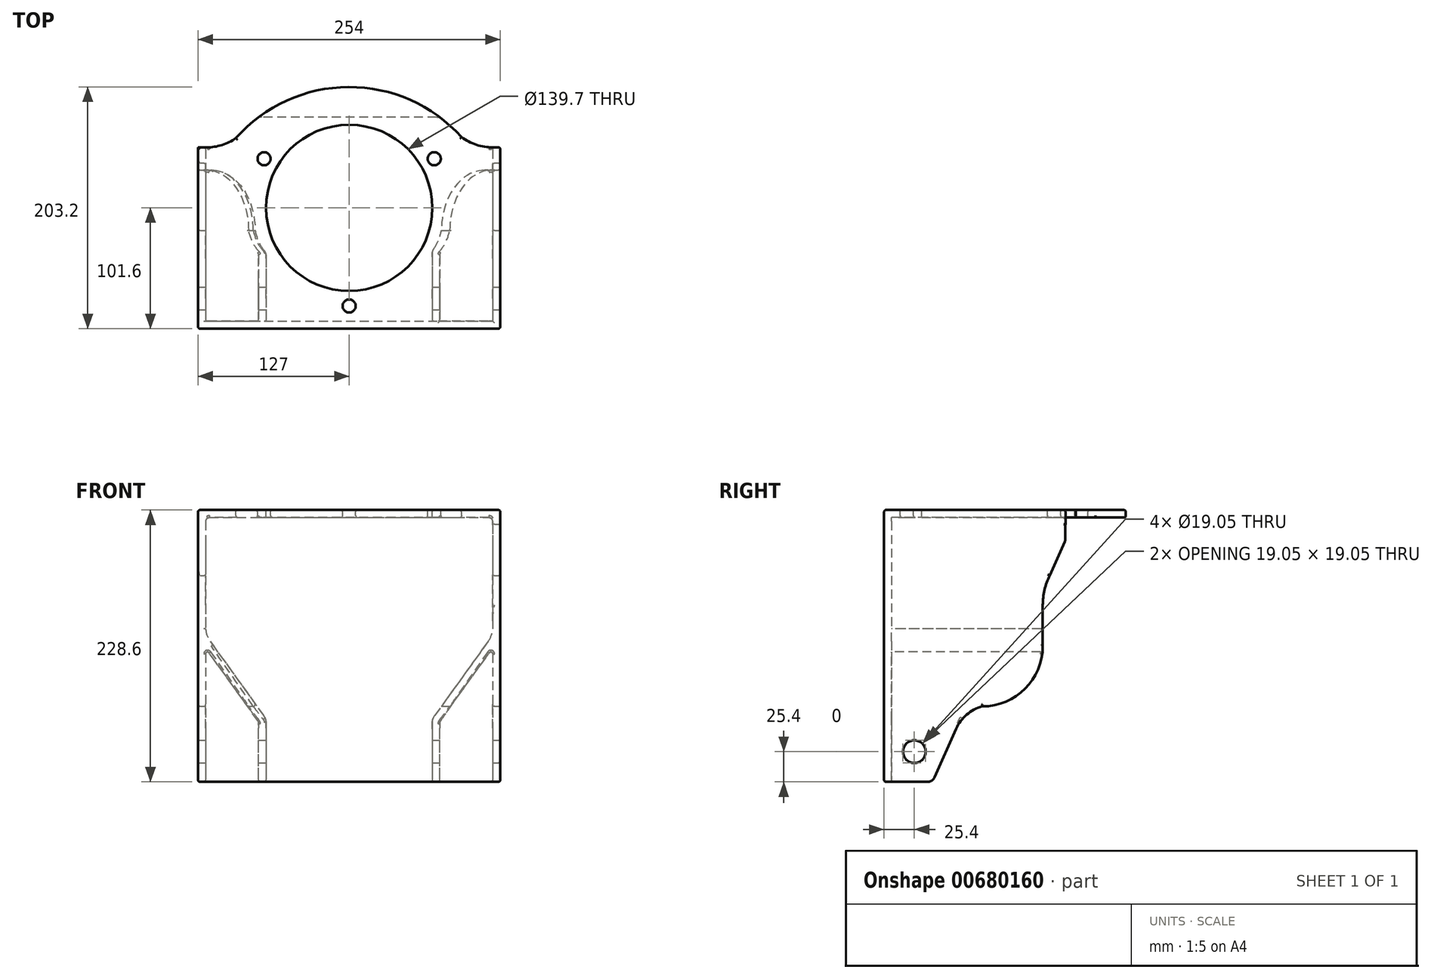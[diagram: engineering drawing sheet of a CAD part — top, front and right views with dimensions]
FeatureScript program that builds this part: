
annotation { "Feature Type Name" : "Feature", "Feature Type Description" : "" }
export const myFeature = defineFeature(function(context is Context, id is Id, definition is map)
    precondition{}
    {
        {
            var Q0;
            Q0=qCreatedBy(makeId("Right.planeOp"),FACE);
            var sketch = newSketch(context, id + "F0", { "sketchPlane" : qUnion([Q0])});
            skLineSegment(sketch, "E0", {"start": v(75.65, 74.97) * mm, "end": v(63.05, 46.62) * mm});
            skLineSegment(sketch, "E1", {"start": v(57.15, 21.64) * mm, "end": v(57.15, -12.7) * mm});
            skLineSegment(sketch, "E2", {"start": v(-39.56, -127) * mm, "end": v(-76.2, -127) * mm});
            skLineSegment(sketch, "E3", {"start": v(-76.2, -127) * mm, "end": v(-76.2, 101.6) * mm});
            skLineSegment(sketch, "E4", {"start": v(-76.2, 101.6) * mm, "end": v(127, 101.6) * mm});
            skLineSegment(sketch, "E5", {"start": v(76.2, 88.88) * mm, "end": v(76.2, 77.55) * mm});
            skArc(sketch, "E6.filletArc", {"start": v(6.35, -63.5) * mm, "mid": v(42.27, -48.62) * mm, "end": v(57.15, -12.7) * mm});
            skLineSegment(sketch, "E7", {"start": v(-15.7, -82.38) * mm, "end": v(-33.75, -123.22) * mm});
            skArc(sketch, "E8.filletArc", {"start": v(-39.56, -127) * mm, "mid": v(-36.1, -125.97) * mm, "end": v(-33.75, -123.22) * mm});
            skPoint(sketch, "E9.visualSharp", {"position": v(76.2, 76.2) * mm});
            skPoint(sketch, "E10.visualSharp", {"position": v(76.2, 101.6) * mm});
            skArc(sketch, "E11", {"start": v(57.15, 21.64) * mm, "mid": v(58.65, 34.47) * mm, "end": v(63.05, 46.62) * mm});
            skArc(sketch, "E12", {"start": v(-15.7, -82.38) * mm, "mid": v(-6.81, -70.44) * mm, "end": v(6.35, -63.5) * mm});
            skArc(sketch, "E13", {"start": v(75.65, 74.97) * mm, "mid": v(76.06, 76.23) * mm, "end": v(76.2, 77.55) * mm});
            skLineSegment(sketch, "E14", {"start": v(82.55, 95.23) * mm, "end": v(127, 95.23) * mm});
            skLineSegment(sketch, "E15", {"start": v(127, 95.23) * mm, "end": v(127, 101.6) * mm});
            skPoint(sketch, "E16.visualSharp", {"position": v(76.2, 95.23) * mm});
            skArc(sketch, "E16.filletArc", {"start": v(82.55, 95.23) * mm, "mid": v(78.06, 93.37) * mm, "end": v(76.2, 88.88) * mm});
            skSolve(sketch);
        }
        {
            var Q0;
            Q0 = qSketchRegion(id + "F0", true);
            extrude(context, id + "F1", {"entities" : qUnion([Q0]), "endBound" : BoundingType.SYMMETRIC, "oppositeDirection" : true, "depth" : 254 * mm, "offsetDistance" : 25.4 * mm});
        }
        {
            var Q0;
            Q0=qCreatedBy(makeId("Front.planeOp"),FACE);
            var sketch = newSketch(context, id + "F2", { "sketchPlane" : qUnion([Q0])});
            skLineSegment(sketch, "E17", {"start": v(120.65, 92.08) * mm, "end": v(120.65, 1.64) * mm});
            skLineSegment(sketch, "E18", {"start": v(116.8, -8.9) * mm, "end": v(71.05, -72.5) * mm});
            skLineSegment(sketch, "E19", {"start": v(69.85, -76.2) * mm, "end": v(69.85, -127) * mm});
            skLineSegment(sketch, "E20", {"start": v(69.85, -127) * mm, "end": v(0, -127) * mm});
            skArc(sketch, "E21", {"start": v(69.85, -76.2) * mm, "mid": v(70.16, -74.25) * mm, "end": v(71.05, -72.5) * mm});
            skArc(sketch, "E22", {"start": v(116.8, -8.9) * mm, "mid": v(119.45, -3.9) * mm, "end": v(120.65, 1.64) * mm});
            skArc(sketch, "E23.MirrorCS", {"start": v(-116.8, -8.9) * mm, "mid": v(-119.45, -3.9) * mm, "end": v(-120.65, 1.64) * mm});
            skArc(sketch, "E24.MirrorCS", {"start": v(-69.85, -76.2) * mm, "mid": v(-70.16, -74.25) * mm, "end": v(-71.05, -72.5) * mm});
            skLineSegment(sketch, "E25.MirrorCS", {"start": v(-69.85, -127) * mm, "end": v(0, -127) * mm});
            skLineSegment(sketch, "E26.MirrorCS", {"start": v(-69.85, -76.2) * mm, "end": v(-69.85, -127) * mm});
            skLineSegment(sketch, "E27.MirrorCS", {"start": v(-116.8, -8.9) * mm, "end": v(-71.05, -72.5) * mm});
            skLineSegment(sketch, "E28.MirrorCS", {"start": v(-120.65, 92.08) * mm, "end": v(-120.65, 1.64) * mm});
            skLineSegment(sketch, "E29", {"start": v(-117.48, 95.25) * mm, "end": v(117.47, 95.25) * mm});
            skArc(sketch, "E30", {"start": v(120.65, 92.08) * mm, "mid": v(119.72, 94.32) * mm, "end": v(117.47, 95.25) * mm});
            skArc(sketch, "E31", {"start": v(-120.65, 92.08) * mm, "mid": v(-119.72, 94.32) * mm, "end": v(-117.48, 95.25) * mm});
            skSolve(sketch);
        }
        {
            var Q0;
            Q0 = qSketchRegion(id + "F2", true);
            extrude(context, id + "F3", {"entities" : qUnion([Q0]), "operationType" : NewBodyOperationType.REMOVE, "endBound" : BoundingType.SYMMETRIC, "oppositeDirection" : true, "depth" : 139.7 * mm, "offsetDistance" : 25.4 * mm});
        }
        {
            var Q0;
            Q0 = qSketchRegion(id + "F2", true);
            extrude(context, id + "F4", {"entities" : qUnion([Q0]), "operationType" : NewBodyOperationType.REMOVE, "oppositeDirection" : true, "depth" : 101.6 * mm, "offsetDistance" : 25.4 * mm});
        }
        {
            var Q0;
            Q0=makeQuery(id+"F1.opExtrude","SWEPT_FACE",FACE,{"disambiguationData":[OSD([sQuery(id+"F0.wireOp",EDGE,"E4")])]});
            var sketch = newSketch(context, id + "F5", { "sketchPlane" : qUnion([Q0])});
            skArc(sketch, "E32", {"start": v(94.46, 84.9) * mm, "mid": v(-0.55, 127) * mm, "end": v(-95.19, 84.07) * mm});
            skLineSegment(sketch, "E33", {"start": v(-127.06, 76.2) * mm, "end": v(-119.85, 76.2) * mm});
            skArc(sketch, "E34", {"start": v(-119.85, 76.2) * mm, "mid": v(-106.9, 78.22) * mm, "end": v(-95.19, 84.07) * mm});
            skLineSegment(sketch, "E35", {"start": v(127.01, 76.25) * mm, "end": v(120.8, 76.25) * mm});
            skArc(sketch, "E36", {"start": v(120.8, 76.25) * mm, "mid": v(106.94, 78.46) * mm, "end": v(94.46, 84.9) * mm});
            skLineSegment(sketch, "E37", {"start": v(-127.06, 76.2) * mm, "end": v(-127, 127) * mm});
            skLineSegment(sketch, "E38", {"start": v(-127, 127) * mm, "end": v(127, 127) * mm});
            skLineSegment(sketch, "E39", {"start": v(127, 127) * mm, "end": v(127.01, 76.25) * mm});
            skSolve(sketch);
        }
        {
            var Q0;
            Q0 = qSketchRegion(id + "F5", true);
            extrude(context, id + "F6", {"entities" : qUnion([Q0]), "operationType" : NewBodyOperationType.REMOVE, "oppositeDirection" : true, "depth" : 19.05 * mm, "offsetDistance" : 25.4 * mm});
        }
        {
            var Q0;
            Q0=qCreatedBy(makeId("Front.planeOp"),FACE);
            var sketch = newSketch(context, id + "F7", { "sketchPlane" : qUnion([Q0])});
            skLineSegment(sketch, "E40", {"start": v(120.65, -19.35) * mm, "end": v(120.65, -135.84) * mm});
            skLineSegment(sketch, "E41", {"start": v(120.65, -135.84) * mm, "end": v(76.2, -135.84) * mm});
            skLineSegment(sketch, "E42", {"start": v(76.2, -135.84) * mm, "end": v(76.2, -77.22) * mm});
            skLineSegment(sketch, "E43", {"start": v(76.8, -75.37) * mm, "end": v(117.77, -18.42) * mm});
            skPoint(sketch, "E44.visualSharp", {"position": v(120.65, -14.42) * mm});
            skArc(sketch, "E44.filletArc", {"start": v(120.65, -19.35) * mm, "mid": v(119.55, -17.84) * mm, "end": v(117.77, -18.42) * mm});
            skPoint(sketch, "E45.visualSharp", {"position": v(76.2, -76.2) * mm});
            skArc(sketch, "E45.filletArc", {"start": v(76.8, -75.37) * mm, "mid": v(76.35, -76.25) * mm, "end": v(76.2, -77.22) * mm});
            skArc(sketch, "E46.MirrorCS", {"start": v(-120.65, -19.35) * mm, "mid": v(-119.55, -17.84) * mm, "end": v(-117.77, -18.42) * mm});
            skArc(sketch, "E47.MirrorCS", {"start": v(-76.8, -75.37) * mm, "mid": v(-76.35, -76.25) * mm, "end": v(-76.2, -77.22) * mm});
            skLineSegment(sketch, "E48.MirrorCS", {"start": v(-120.65, -135.84) * mm, "end": v(-76.2, -135.84) * mm});
            skPoint(sketch, "E49.MirrorP", {"position": v(-76.2, -76.2) * mm});
            skLineSegment(sketch, "E50.MirrorCS", {"start": v(-120.65, -19.35) * mm, "end": v(-120.65, -135.84) * mm});
            skPoint(sketch, "E51.MirrorP", {"position": v(-120.65, -14.42) * mm});
            skLineSegment(sketch, "E52.MirrorCS", {"start": v(-76.8, -75.37) * mm, "end": v(-117.77, -18.42) * mm});
            skLineSegment(sketch, "E53.MirrorCS", {"start": v(-76.2, -135.84) * mm, "end": v(-76.2, -77.22) * mm});
            skSolve(sketch);
        }
        {
            var Q0;
            Q0 = qSketchRegion(id + "F7", true);
            extrude(context, id + "F8", {"entities" : qUnion([Q0]), "operationType" : NewBodyOperationType.REMOVE, "endBound" : BoundingType.SYMMETRIC, "oppositeDirection" : true, "depth" : 139.7 * mm, "offsetDistance" : 25.4 * mm});
        }
        {
            var Q0;
            Q0=makeQuery(id+"F1.opExtrude","SWEPT_FACE",FACE,{"disambiguationData":[OSD([sQuery(id+"F0.wireOp",EDGE,"E4")])]});
            var sketch = newSketch(context, id + "F9", { "sketchPlane" : qUnion([Q0])});
            skCircle(sketch, "E54", {"center": v(0, 25.4) * mm, "radius": 69.85 * mm});
            skCircle(sketch, "E55", {"center": v(-71.5, 66.68) * mm, "radius": 5.52 * mm});
            skCircle(sketch, "E56", {"center": v(71.5, 66.67) * mm, "radius": 5.52 * mm});
            skCircle(sketch, "E57", {"center": v(0, -57.15) * mm, "radius": 5.52 * mm});
            skSolve(sketch);
        }
        {
            var Q0;
            Q0 = qSketchRegion(id + "F9", true);
            extrude(context, id + "F10", {"entities" : qUnion([Q0]), "operationType" : NewBodyOperationType.REMOVE, "oppositeDirection" : true, "depth" : 6.86 * mm, "offsetDistance" : 25.4 * mm});
        }
        {
            var Q0;
            Q0=makeQuery(id+"F1.opExtrude","CAP_FACE",FACE,{"disambiguationData":[OSD([sQuery(id+"F0.wireOp",EDGE,"E0"),sQuery(id+"F0.wireOp",EDGE,"E1"),sQuery(id+"F0.wireOp",EDGE,"E2"),sQuery(id+"F0.wireOp",EDGE,"E3"),sQuery(id+"F0.wireOp",EDGE,"E4"),sQuery(id+"F0.wireOp",EDGE,"E5"),sQuery(id+"F0.wireOp",EDGE,"E6.filletArc"),sQuery(id+"F0.wireOp",EDGE,"E7"),sQuery(id+"F0.wireOp",EDGE,"E8.filletArc"),sQuery(id+"F0.wireOp",EDGE,"E11"),sQuery(id+"F0.wireOp",EDGE,"E12"),sQuery(id+"F0.wireOp",EDGE,"E13"),sQuery(id+"F0.wireOp",EDGE,"E14"),sQuery(id+"F0.wireOp",EDGE,"E15"),sQuery(id+"F0.wireOp",EDGE,"E16.filletArc")])],"isStart":true});
            var sketch = newSketch(context, id + "F11", { "sketchPlane" : qUnion([Q0])});
            skCircle(sketch, "E58", {"center": v(-50.8, -101.6) * mm, "radius": 9.53 * mm});
            skSolve(sketch);
        }
        {
            var Q0;
            Q0 = qSketchRegion(id + "F11", true);
            extrude(context, id + "F12", {"entities" : qUnion([Q0]), "operationType" : NewBodyOperationType.REMOVE, "endBound" : BoundingType.THROUGH_ALL, "oppositeDirection" : true, "depth" : 25.4 * mm, "offsetDistance" : 25.4 * mm});
        }
        {
            var Q0;
            Q0=makeQuery(id+"F10.boolean.opBoolean","COPY",EDGE,{"derivedFrom":makeQuery(id+"F10.opExtrude","CAP_EDGE",EDGE,{"disambiguationData":[OSD([sQuery(id+"F9.wireOp",EDGE,"E54")])],"isStart":true})});
            var Q1;
            Q1=makeQuery(id+"F10.boolean.opBoolean","COPY",EDGE,{"derivedFrom":makeQuery(id+"F10.opExtrude","CAP_EDGE",EDGE,{"disambiguationData":[OSD([sQuery(id+"F9.wireOp",EDGE,"E55")])],"isStart":true})});
            var Q2;
            Q2=makeQuery(id+"F10.boolean.opBoolean","COPY",EDGE,{"derivedFrom":makeQuery(id+"F10.opExtrude","CAP_EDGE",EDGE,{"disambiguationData":[OSD([sQuery(id+"F9.wireOp",EDGE,"E56")])],"isStart":true})});
            var Q3;
            {var subQ0=sQuery(id+"F2.wireOp",EDGE,"E29");Q3=makeQuery(id+"F10.boolean.opBoolean","INTERSECT",EDGE,{"derivedFrom":[makeQuery(id+"F4.boolean.opBoolean","MERGE",FACE,{"derivedFrom":[makeQuery(id+"F3.boolean.opBoolean","COPY",FACE,{"derivedFrom":makeQuery(id+"F3.opExtrude","SWEPT_FACE",FACE,{"disambiguationData":[OSD([subQ0])]})}),makeQuery(id+"F4.opExtrude","SWEPT_FACE",FACE,{"disambiguationData":[OSD([subQ0])]})]}),makeQuery(id+"F10.opExtrude","SWEPT_FACE",FACE,{"disambiguationData":[OSD([sQuery(id+"F9.wireOp",EDGE,"E56")])]})]});}
            var Q4;
            Q4=makeQuery(id+"F10.boolean.opBoolean","COPY",EDGE,{"derivedFrom":makeQuery(id+"F10.opExtrude","CAP_EDGE",EDGE,{"disambiguationData":[OSD([sQuery(id+"F9.wireOp",EDGE,"E57")])],"isStart":true})});
            var Q5;
            {var subQ0=sQuery(id+"F2.wireOp",EDGE,"E29");Q5=makeQuery(id+"F10.boolean.opBoolean","INTERSECT",EDGE,{"derivedFrom":[makeQuery(id+"F4.boolean.opBoolean","MERGE",FACE,{"derivedFrom":[makeQuery(id+"F3.boolean.opBoolean","COPY",FACE,{"derivedFrom":makeQuery(id+"F3.opExtrude","SWEPT_FACE",FACE,{"disambiguationData":[OSD([subQ0])]})}),makeQuery(id+"F4.opExtrude","SWEPT_FACE",FACE,{"disambiguationData":[OSD([subQ0])]})]}),makeQuery(id+"F10.opExtrude","SWEPT_FACE",FACE,{"disambiguationData":[OSD([sQuery(id+"F9.wireOp",EDGE,"E57")])]})]});}
            var Q6;
            {var subQ0=sQuery(id+"F2.wireOp",EDGE,"E29");Q6=makeQuery(id+"F10.boolean.opBoolean","INTERSECT",EDGE,{"derivedFrom":[makeQuery(id+"F4.boolean.opBoolean","MERGE",FACE,{"derivedFrom":[makeQuery(id+"F3.boolean.opBoolean","COPY",FACE,{"derivedFrom":makeQuery(id+"F3.opExtrude","SWEPT_FACE",FACE,{"disambiguationData":[OSD([subQ0])]})}),makeQuery(id+"F4.opExtrude","SWEPT_FACE",FACE,{"disambiguationData":[OSD([subQ0])]})]}),makeQuery(id+"F10.opExtrude","SWEPT_FACE",FACE,{"disambiguationData":[OSD([sQuery(id+"F9.wireOp",EDGE,"E55")])]})]});}
            var Q7;
            Q7=makeQuery(id+"F1.opExtrude","CAP_EDGE",EDGE,{"disambiguationData":[OSD([sQuery(id+"F0.wireOp",EDGE,"E4")])],"isStart":true});
            var Q8;
            Q8=makeQuery(id+"F1.opExtrude","SWEPT_EDGE",EDGE,{"disambiguationData":[OSD([sQuery(id+"F0.wireOp",EDGE,"E3"),sQuery(id+"F0.wireOp",EDGE,"E4")])]});
            var Q9;
            Q9=makeQuery(id+"F1.opExtrude","CAP_EDGE",EDGE,{"disambiguationData":[OSD([sQuery(id+"F0.wireOp",EDGE,"E4")])],"isStart":false});
            var Q10;
            Q10=makeQuery(id+"F6.boolean.opBoolean","COPY",EDGE,{"derivedFrom":makeQuery(id+"F6.opExtrude","CAP_EDGE",EDGE,{"disambiguationData":[OSD([sQuery(id+"F5.wireOp",EDGE,"E33")])],"isStart":true})});
            var Q11;
            Q11=makeQuery(id+"F1.opExtrude","SWEPT_FACE",FACE,{"disambiguationData":[OSD([sQuery(id+"F0.wireOp",EDGE,"E4")])]});
            var Q12;
            {var subQ0=sQuery(id+"F2.wireOp",EDGE,"E30");Q12=makeQuery(id+"F6.boolean.opBoolean","INTERSECT",EDGE,{"derivedFrom":[makeQuery(id+"F4.boolean.opBoolean","MERGE",FACE,{"derivedFrom":[makeQuery(id+"F3.boolean.opBoolean","COPY",FACE,{"derivedFrom":makeQuery(id+"F3.opExtrude","SWEPT_FACE",FACE,{"disambiguationData":[OSD([subQ0])]})}),makeQuery(id+"F4.opExtrude","SWEPT_FACE",FACE,{"disambiguationData":[OSD([subQ0])]})]}),makeQuery(id+"F6.opExtrude","SWEPT_FACE",FACE,{"disambiguationData":[OSD([sQuery(id+"F5.wireOp",EDGE,"E36")])]})]});}
            var Q13;
            {var subQ0=sQuery(id+"F2.wireOp",EDGE,"E29");Q13=makeQuery(id+"F6.boolean.opBoolean","INTERSECT",EDGE,{"derivedFrom":[makeQuery(id+"F4.boolean.opBoolean","MERGE",FACE,{"derivedFrom":[makeQuery(id+"F3.boolean.opBoolean","COPY",FACE,{"derivedFrom":makeQuery(id+"F3.opExtrude","SWEPT_FACE",FACE,{"disambiguationData":[OSD([subQ0])]})}),makeQuery(id+"F4.opExtrude","SWEPT_FACE",FACE,{"disambiguationData":[OSD([subQ0])]})]}),makeQuery(id+"F6.opExtrude","SWEPT_FACE",FACE,{"disambiguationData":[OSD([sQuery(id+"F5.wireOp",EDGE,"E36")])]})]});}
            var Q14;
            Q14=makeQuery(id+"F4.boolean.opBoolean","INTERSECT",EDGE,{"derivedFrom":[makeQuery(id+"F1.opExtrude","SWEPT_FACE",FACE,{"disambiguationData":[OSD([sQuery(id+"F0.wireOp",EDGE,"E0")])]}),makeQuery(id+"F4.opExtrude","SWEPT_FACE",FACE,{"disambiguationData":[OSD([sQuery(id+"F2.wireOp",EDGE,"E17")])]})]});
            var Q15;
            Q15=makeQuery(id+"F1.opExtrude","CAP_FACE",FACE,{"disambiguationData":[OSD([sQuery(id+"F0.wireOp",EDGE,"E0"),sQuery(id+"F0.wireOp",EDGE,"E1"),sQuery(id+"F0.wireOp",EDGE,"E2"),sQuery(id+"F0.wireOp",EDGE,"E3"),sQuery(id+"F0.wireOp",EDGE,"E4"),sQuery(id+"F0.wireOp",EDGE,"E5"),sQuery(id+"F0.wireOp",EDGE,"E6.filletArc"),sQuery(id+"F0.wireOp",EDGE,"E7"),sQuery(id+"F0.wireOp",EDGE,"E8.filletArc"),sQuery(id+"F0.wireOp",EDGE,"E11"),sQuery(id+"F0.wireOp",EDGE,"E12"),sQuery(id+"F0.wireOp",EDGE,"E13"),sQuery(id+"F0.wireOp",EDGE,"E14"),sQuery(id+"F0.wireOp",EDGE,"E15"),sQuery(id+"F0.wireOp",EDGE,"E16.filletArc")])],"isStart":true});
            var Q16;
            Q16=makeQuery(id+"F8.boolean.opBoolean","INTERSECT",EDGE,{"derivedFrom":[makeQuery(id+"F1.opExtrude","SWEPT_FACE",FACE,{"disambiguationData":[OSD([sQuery(id+"F0.wireOp",EDGE,"E2")])]}),makeQuery(id+"F8.opExtrude","CAP_FACE",FACE,{"disambiguationData":[OSD([sQuery(id+"F7.wireOp",EDGE,"E40"),sQuery(id+"F7.wireOp",EDGE,"E41"),sQuery(id+"F7.wireOp",EDGE,"E42"),sQuery(id+"F7.wireOp",EDGE,"E43"),sQuery(id+"F7.wireOp",EDGE,"E44.filletArc"),sQuery(id+"F7.wireOp",EDGE,"E45.filletArc")])],"isStart":true})]});
            var Q17;
            Q17=makeQuery(id+"F8.boolean.opBoolean","INTERSECT",EDGE,{"derivedFrom":[makeQuery(id+"F1.opExtrude","SWEPT_FACE",FACE,{"disambiguationData":[OSD([sQuery(id+"F0.wireOp",EDGE,"E2")])]}),makeQuery(id+"F8.opExtrude","SWEPT_FACE",FACE,{"disambiguationData":[OSD([sQuery(id+"F7.wireOp",EDGE,"E40")])]})]});
            var Q18;
            Q18=makeQuery(id+"F1.opExtrude","SWEPT_EDGE",EDGE,{"disambiguationData":[OSD([sQuery(id+"F0.wireOp",EDGE,"E2"),sQuery(id+"F0.wireOp",EDGE,"E3")])]});
            var Q19;
            {var subQ1=sQuery(id+"F0.wireOp",EDGE,"E6.filletArc");Q19=makeQuery(id+"F8.boolean.opBoolean","INTERSECT",EDGE,{"derivedFrom":[makeQuery(id+"F3.boolean.opBoolean","SPLIT",FACE,{"disambiguationData":[TD([makeQuery(id+"F3.opExtrude","SWEPT_FACE",FACE,{"disambiguationData":[OSD([sQuery(id+"F2.wireOp",EDGE,"E18")])]})])],"derivedFrom":makeQuery(id+"F1.opExtrude","SWEPT_FACE",FACE,{"disambiguationData":[OSD([subQ1])]})}),makeQuery(id+"F8.opExtrude","SWEPT_FACE",FACE,{"disambiguationData":[OSD([sQuery(id+"F7.wireOp",EDGE,"E40")])]})]});}
            var Q20;
            {var subQ2=sQuery(id+"F0.wireOp",EDGE,"E12");Q20=makeQuery(id+"F8.boolean.opBoolean","INTERSECT",EDGE,{"derivedFrom":[makeQuery(id+"F3.boolean.opBoolean","SPLIT",FACE,{"disambiguationData":[TD([makeQuery(id+"F3.opExtrude","SWEPT_FACE",FACE,{"disambiguationData":[OSD([sQuery(id+"F2.wireOp",EDGE,"E18")])]})])],"derivedFrom":makeQuery(id+"F1.opExtrude","SWEPT_FACE",FACE,{"disambiguationData":[OSD([subQ2])]})}),makeQuery(id+"F8.opExtrude","SWEPT_FACE",FACE,{"disambiguationData":[OSD([sQuery(id+"F7.wireOp",EDGE,"E43")])]})]});}
            var Q21;
            Q21=makeQuery(id+"F1.opExtrude","CAP_EDGE",EDGE,{"disambiguationData":[OSD([sQuery(id+"F0.wireOp",EDGE,"E3")])],"isStart":false});
            var Q22;
            Q22=makeQuery(id+"F1.opExtrude","CAP_EDGE",EDGE,{"disambiguationData":[OSD([sQuery(id+"F0.wireOp",EDGE,"E2")])],"isStart":false});
            var Q23;
            Q23=makeQuery(id+"F1.opExtrude","CAP_EDGE",EDGE,{"disambiguationData":[OSD([sQuery(id+"F0.wireOp",EDGE,"E6.filletArc")])],"isStart":false});
            var Q24;
            {var subQ0=sQuery(id+"F5.wireOp",EDGE,"E32");var subQ1=sQuery(id+"F2.wireOp",EDGE,"E29");Q24=makeQuery(id+"F6.boolean.opBoolean","INTERSECT",EDGE,{"derivedFrom":[makeQuery(id+"F4.boolean.opBoolean","MERGE",FACE,{"derivedFrom":[makeQuery(id+"F3.boolean.opBoolean","COPY",FACE,{"derivedFrom":makeQuery(id+"F3.opExtrude","SWEPT_FACE",FACE,{"disambiguationData":[OSD([subQ1])]})}),makeQuery(id+"F4.opExtrude","SWEPT_FACE",FACE,{"disambiguationData":[OSD([subQ1])]})]}),makeQuery(id+"F6.opExtrude","SWEPT_FACE",FACE,{"disambiguationData":[OSD([subQ0]),TDD([makeQuery(id+"F5.imprint","IMPRINT",EDGE,{"disambiguationData":[TD([[makeQuery(id+"F5.imprint","INTERSECT",VERTEX,{"derivedFrom":[subQ0,sQuery(id+"F5.wireOp",EDGE,"E36")]}),-1.0]])],"derivedFrom":subQ0})])]})]});}
            var Q25;
            {var subQ0=sQuery(id+"F5.wireOp",EDGE,"E32");var subQ2=sQuery(id+"F2.wireOp",EDGE,"E29");Q25=makeQuery(id+"F6.boolean.opBoolean","INTERSECT",EDGE,{"derivedFrom":[makeQuery(id+"F4.boolean.opBoolean","MERGE",FACE,{"derivedFrom":[makeQuery(id+"F3.boolean.opBoolean","COPY",FACE,{"derivedFrom":makeQuery(id+"F3.opExtrude","SWEPT_FACE",FACE,{"disambiguationData":[OSD([subQ2])]})}),makeQuery(id+"F4.opExtrude","SWEPT_FACE",FACE,{"disambiguationData":[OSD([subQ2])]})]}),makeQuery(id+"F6.opExtrude","SWEPT_FACE",FACE,{"disambiguationData":[OSD([subQ0]),TDD([makeQuery(id+"F5.imprint","IMPRINT",EDGE,{"disambiguationData":[TD([[makeQuery(id+"F5.imprint","INTERSECT",VERTEX,{"derivedFrom":[subQ0,sQuery(id+"F5.wireOp",EDGE,"E36")]}),-1.0]])],"derivedFrom":subQ0})])]}),makeQuery(id+"F6.opExtrude","SWEPT_FACE",FACE,{"disambiguationData":[OSD([subQ0]),TDD([makeQuery(id+"F5.imprint","IMPRINT",EDGE,{"disambiguationData":[TD([[makeQuery(id+"F5.imprint","INTERSECT",VERTEX,{"derivedFrom":[subQ0,sQuery(id+"F5.wireOp",EDGE,"E34")]}),1.0]])],"derivedFrom":subQ0})])]})]});}
            var Q26;
            {var subQ0=sQuery(id+"F2.wireOp",EDGE,"E28.MirrorCS");Q26=makeQuery(id+"F6.boolean.opBoolean","INTERSECT",EDGE,{"derivedFrom":[makeQuery(id+"F4.boolean.opBoolean","MERGE",FACE,{"derivedFrom":[makeQuery(id+"F3.boolean.opBoolean","COPY",FACE,{"derivedFrom":makeQuery(id+"F3.opExtrude","SWEPT_FACE",FACE,{"disambiguationData":[OSD([subQ0])]})}),makeQuery(id+"F4.opExtrude","SWEPT_FACE",FACE,{"disambiguationData":[OSD([subQ0])]})]}),makeQuery(id+"F6.opExtrude","SWEPT_FACE",FACE,{"disambiguationData":[OSD([sQuery(id+"F5.wireOp",EDGE,"E33")])]})]});}
            var Q27;
            Q27=makeQuery(id+"F4.boolean.opBoolean","INTERSECT",EDGE,{"derivedFrom":[makeQuery(id+"F1.opExtrude","SWEPT_FACE",FACE,{"disambiguationData":[OSD([sQuery(id+"F0.wireOp",EDGE,"E0")])]}),makeQuery(id+"F4.opExtrude","SWEPT_FACE",FACE,{"disambiguationData":[OSD([sQuery(id+"F2.wireOp",EDGE,"E28.MirrorCS")])]})]});
            var Q28;
            Q28=makeQuery(id+"F3.boolean.opBoolean","INTERSECT",EDGE,{"derivedFrom":[makeQuery(id+"F1.opExtrude","SWEPT_FACE",FACE,{"disambiguationData":[OSD([sQuery(id+"F0.wireOp",EDGE,"E11")])]}),makeQuery(id+"F3.opExtrude","SWEPT_FACE",FACE,{"disambiguationData":[OSD([sQuery(id+"F2.wireOp",EDGE,"E28.MirrorCS")])]})]});
            var Q29;
            Q29=makeQuery(id+"F3.boolean.opBoolean","INTERSECT",EDGE,{"derivedFrom":[makeQuery(id+"F1.opExtrude","SWEPT_FACE",FACE,{"disambiguationData":[OSD([sQuery(id+"F0.wireOp",EDGE,"E7")])]}),makeQuery(id+"F3.opExtrude","SWEPT_FACE",FACE,{"disambiguationData":[OSD([sQuery(id+"F2.wireOp",EDGE,"E26.MirrorCS")])]})]});
            var Q30;
            {var subQ2=sQuery(id+"F0.wireOp",EDGE,"E7");Q30=makeQuery(id+"F8.boolean.opBoolean","INTERSECT",EDGE,{"derivedFrom":[makeQuery(id+"F3.boolean.opBoolean","SPLIT",FACE,{"disambiguationData":[TD([makeQuery(id+"F3.opExtrude","SWEPT_FACE",FACE,{"disambiguationData":[OSD([sQuery(id+"F2.wireOp",EDGE,"E19")])]})])],"derivedFrom":makeQuery(id+"F1.opExtrude","SWEPT_FACE",FACE,{"disambiguationData":[OSD([subQ2])]})}),makeQuery(id+"F8.opExtrude","SWEPT_FACE",FACE,{"disambiguationData":[OSD([sQuery(id+"F7.wireOp",EDGE,"E42")])]})]});}
            var Q31;
            Q31=makeQuery(id+"F3.boolean.opBoolean","INTERSECT",EDGE,{"derivedFrom":[makeQuery(id+"F1.opExtrude","SWEPT_FACE",FACE,{"disambiguationData":[OSD([sQuery(id+"F0.wireOp",EDGE,"E6.filletArc")])]}),makeQuery(id+"F3.opExtrude","SWEPT_FACE",FACE,{"disambiguationData":[OSD([sQuery(id+"F2.wireOp",EDGE,"E27.MirrorCS")])]})]});
            var Q32;
            {var subQ2=sQuery(id+"F0.wireOp",EDGE,"E12");Q32=makeQuery(id+"F8.boolean.opBoolean","INTERSECT",EDGE,{"derivedFrom":[makeQuery(id+"F3.boolean.opBoolean","SPLIT",FACE,{"disambiguationData":[TD([makeQuery(id+"F3.opExtrude","SWEPT_FACE",FACE,{"disambiguationData":[OSD([sQuery(id+"F2.wireOp",EDGE,"E24.MirrorCS")])]})])],"derivedFrom":makeQuery(id+"F1.opExtrude","SWEPT_FACE",FACE,{"disambiguationData":[OSD([subQ2])]})}),makeQuery(id+"F8.opExtrude","SWEPT_FACE",FACE,{"disambiguationData":[OSD([sQuery(id+"F7.wireOp",EDGE,"E50.MirrorCS")])]})]});}
            var Q33;
            {var subQ2=sQuery(id+"F0.wireOp",EDGE,"E7");Q33=makeQuery(id+"F8.boolean.opBoolean","INTERSECT",EDGE,{"derivedFrom":[makeQuery(id+"F3.boolean.opBoolean","SPLIT",FACE,{"disambiguationData":[TD([makeQuery(id+"F3.opExtrude","SWEPT_FACE",FACE,{"disambiguationData":[OSD([sQuery(id+"F2.wireOp",EDGE,"E26.MirrorCS")])]})])],"derivedFrom":makeQuery(id+"F1.opExtrude","SWEPT_FACE",FACE,{"disambiguationData":[OSD([subQ2])]})}),makeQuery(id+"F8.opExtrude","SWEPT_FACE",FACE,{"disambiguationData":[OSD([sQuery(id+"F7.wireOp",EDGE,"E50.MirrorCS")])]})]});}
            var Q34;
            Q34=makeQuery(id+"F3.boolean.opBoolean","INTERSECT",EDGE,{"derivedFrom":[makeQuery(id+"F1.opExtrude","SWEPT_FACE",FACE,{"disambiguationData":[OSD([sQuery(id+"F0.wireOp",EDGE,"E12")])]}),makeQuery(id+"F3.opExtrude","SWEPT_FACE",FACE,{"disambiguationData":[OSD([sQuery(id+"F2.wireOp",EDGE,"E27.MirrorCS")])]})]});
            var Q35;
            Q35=makeQuery(id+"F3.boolean.opBoolean","INTERSECT",EDGE,{"derivedFrom":[makeQuery(id+"F1.opExtrude","SWEPT_FACE",FACE,{"disambiguationData":[OSD([sQuery(id+"F0.wireOp",EDGE,"E12")])]}),makeQuery(id+"F3.opExtrude","SWEPT_FACE",FACE,{"disambiguationData":[OSD([sQuery(id+"F2.wireOp",EDGE,"E24.MirrorCS")])]})]});
            var Q36;
            Q36=makeQuery(id+"F3.boolean.opBoolean","INTERSECT",EDGE,{"derivedFrom":[makeQuery(id+"F1.opExtrude","SWEPT_FACE",FACE,{"disambiguationData":[OSD([sQuery(id+"F0.wireOp",EDGE,"E12")])]}),makeQuery(id+"F3.opExtrude","SWEPT_FACE",FACE,{"disambiguationData":[OSD([sQuery(id+"F2.wireOp",EDGE,"E26.MirrorCS")])]})]});
            var Q37;
            {var subQ1=sQuery(id+"F0.wireOp",EDGE,"E6.filletArc");Q37=makeQuery(id+"F8.boolean.opBoolean","INTERSECT",EDGE,{"derivedFrom":[makeQuery(id+"F3.boolean.opBoolean","SPLIT",FACE,{"disambiguationData":[TD([makeQuery(id+"F3.opExtrude","SWEPT_FACE",FACE,{"disambiguationData":[OSD([sQuery(id+"F2.wireOp",EDGE,"E27.MirrorCS")])]})])],"derivedFrom":makeQuery(id+"F1.opExtrude","SWEPT_FACE",FACE,{"disambiguationData":[OSD([subQ1])]})}),makeQuery(id+"F8.opExtrude","SWEPT_FACE",FACE,{"disambiguationData":[OSD([sQuery(id+"F7.wireOp",EDGE,"E52.MirrorCS")])]})]});}
            var Q38;
            {var subQ1=sQuery(id+"F0.wireOp",EDGE,"E6.filletArc");Q38=makeQuery(id+"F8.boolean.opBoolean","INTERSECT",EDGE,{"derivedFrom":[makeQuery(id+"F3.boolean.opBoolean","SPLIT",FACE,{"disambiguationData":[TD([makeQuery(id+"F3.opExtrude","SWEPT_FACE",FACE,{"disambiguationData":[OSD([sQuery(id+"F2.wireOp",EDGE,"E27.MirrorCS")])]})])],"derivedFrom":makeQuery(id+"F1.opExtrude","SWEPT_FACE",FACE,{"disambiguationData":[OSD([subQ1])]})}),makeQuery(id+"F8.opExtrude","SWEPT_FACE",FACE,{"disambiguationData":[OSD([sQuery(id+"F7.wireOp",EDGE,"E50.MirrorCS")])]})]});}
            var Q39;
            {var subQ2=sQuery(id+"F0.wireOp",EDGE,"E7");Q39=makeQuery(id+"F8.boolean.opBoolean","INTERSECT",EDGE,{"derivedFrom":[makeQuery(id+"F3.boolean.opBoolean","SPLIT",FACE,{"disambiguationData":[TD([makeQuery(id+"F3.opExtrude","SWEPT_FACE",FACE,{"disambiguationData":[OSD([sQuery(id+"F2.wireOp",EDGE,"E26.MirrorCS")])]})])],"derivedFrom":makeQuery(id+"F1.opExtrude","SWEPT_FACE",FACE,{"disambiguationData":[OSD([subQ2])]})}),makeQuery(id+"F8.opExtrude","SWEPT_FACE",FACE,{"disambiguationData":[OSD([sQuery(id+"F7.wireOp",EDGE,"E53.MirrorCS")])]})]});}
            fillet(context, id + "F13", {"entities" : qUnion([Q0, Q1, Q2, Q3, Q4, Q5, Q6, Q7, Q8, Q9, Q10, Q11, Q12, Q13, Q14, Q15, Q16, Q17, Q18, Q19, Q20, Q21, Q22, Q23, Q24, Q25, Q26, Q27, Q28, Q29, Q30, Q31, Q32, Q33, Q34, Q35, Q36, Q37, Q38, Q39]), "radius" : 1.59 * mm, "tangentPropagation" : true, "allowEdgeOverflow" : false});
        }
        {
            var Q0;
            {var subQ0=sQuery(id+"F5.wireOp",EDGE,"E32");Q0=makeQuery(id+"F6.boolean.opBoolean","INTERSECT",EDGE,{"derivedFrom":[makeQuery(id+"F1.opExtrude","SWEPT_FACE",FACE,{"disambiguationData":[OSD([sQuery(id+"F0.wireOp",EDGE,"E14")])]}),makeQuery(id+"F6.opExtrude","SWEPT_FACE",FACE,{"disambiguationData":[OSD([subQ0]),TDD([makeQuery(id+"F5.imprint","IMPRINT",EDGE,{"disambiguationData":[TD([[makeQuery(id+"F5.imprint","INTERSECT",VERTEX,{"derivedFrom":[subQ0,sQuery(id+"F5.wireOp",EDGE,"E36")]}),-1.0]])],"derivedFrom":subQ0})])]}),makeQuery(id+"F6.opExtrude","SWEPT_FACE",FACE,{"disambiguationData":[OSD([subQ0]),TDD([makeQuery(id+"F5.imprint","IMPRINT",EDGE,{"disambiguationData":[TD([[makeQuery(id+"F5.imprint","INTERSECT",VERTEX,{"derivedFrom":[subQ0,sQuery(id+"F5.wireOp",EDGE,"E34")]}),1.0]])],"derivedFrom":subQ0})])]})]});}
            fillet(context, id + "F14", {"entities" : qUnion([Q0]), "radius" : 1.59 * mm, "tangentPropagation" : true, "allowEdgeOverflow" : false});
        }
    });
